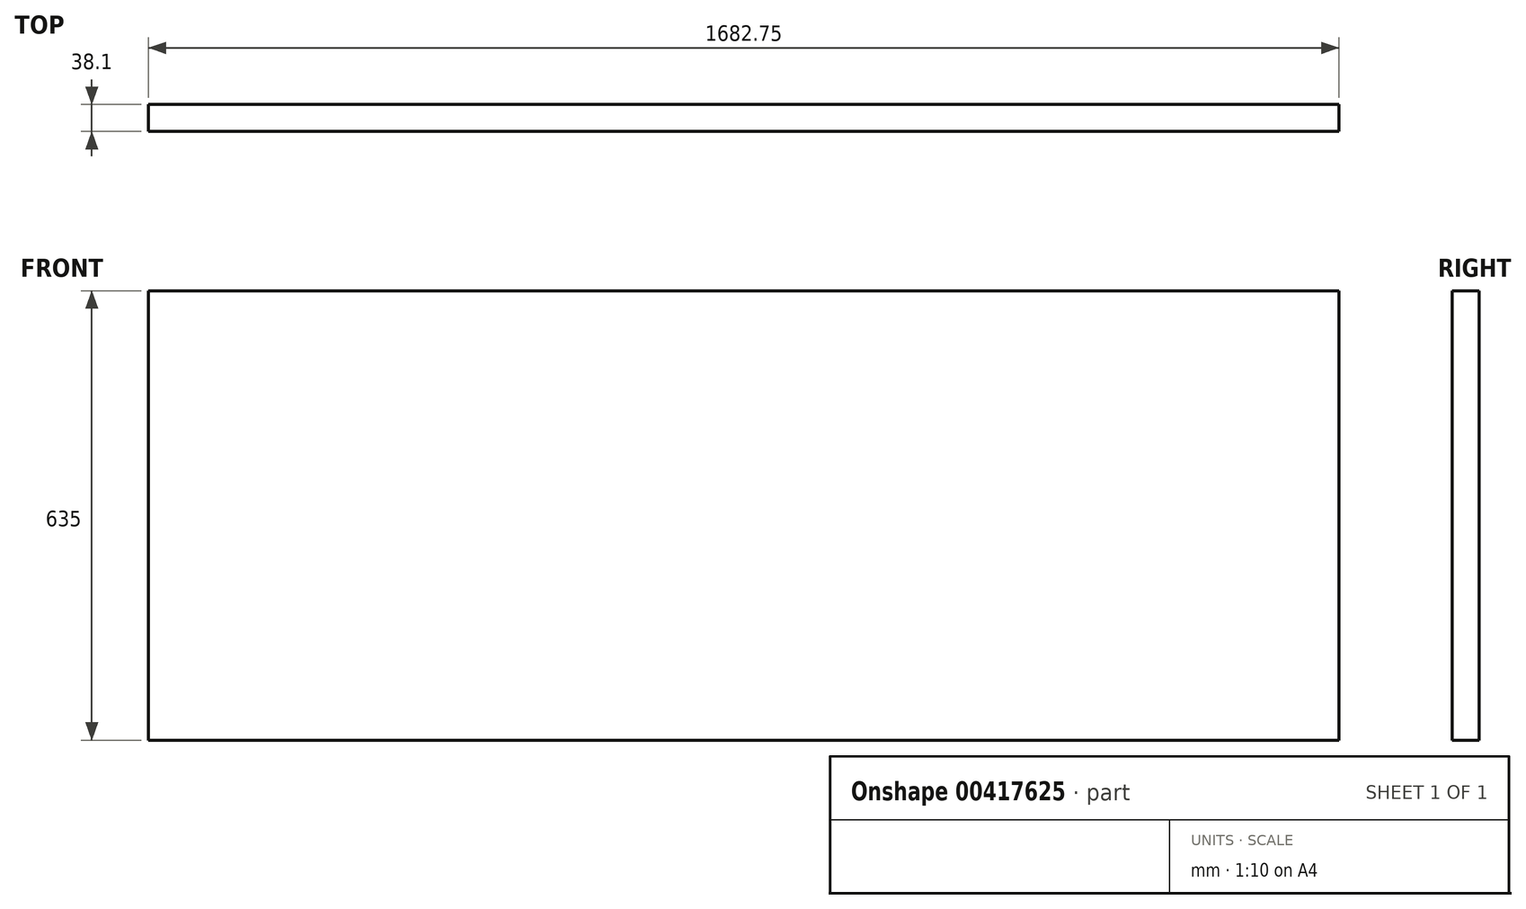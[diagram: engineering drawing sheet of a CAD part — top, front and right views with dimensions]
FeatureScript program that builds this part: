
annotation { "Feature Type Name" : "Feature", "Feature Type Description" : "" }
export const myFeature = defineFeature(function(context is Context, id is Id, definition is map)
    precondition{}
    {
        {
            var Q0;
            Q0=qCreatedBy(makeId("Front.planeOp"),FACE);
            var sketch = newSketch(context, id + "F0", { "sketchPlane" : qUnion([Q0])});
            skLineSegment(sketch, "E0.bottom", {"start": v(0, 0) * mm, "end": v(1682.75, 0) * mm});
            skLineSegment(sketch, "E0.top", {"start": v(0, 635) * mm, "end": v(1682.75, 635) * mm});
            skLineSegment(sketch, "E0.left", {"start": v(0, 0) * mm, "end": v(0, 635) * mm});
            skLineSegment(sketch, "E0.right", {"start": v(1682.75, 0) * mm, "end": v(1682.75, 635) * mm});
            skSolve(sketch);
        }
        {
            var Q0;
            Q0=makeQuery(id+"F0.imprint","IMPRINT",FACE,{"disambiguationData":[TD([[makeQuery(id+"F0.imprint","IMPRINT",EDGE,{"derivedFrom":sQuery(id+"F0.wireOp",EDGE,"E0.bottom")}),1.0]])]});
            extrude(context, id + "F1", {"entities" : qUnion([Q0]), "depth" : 38.1 * mm});
        }
    });
